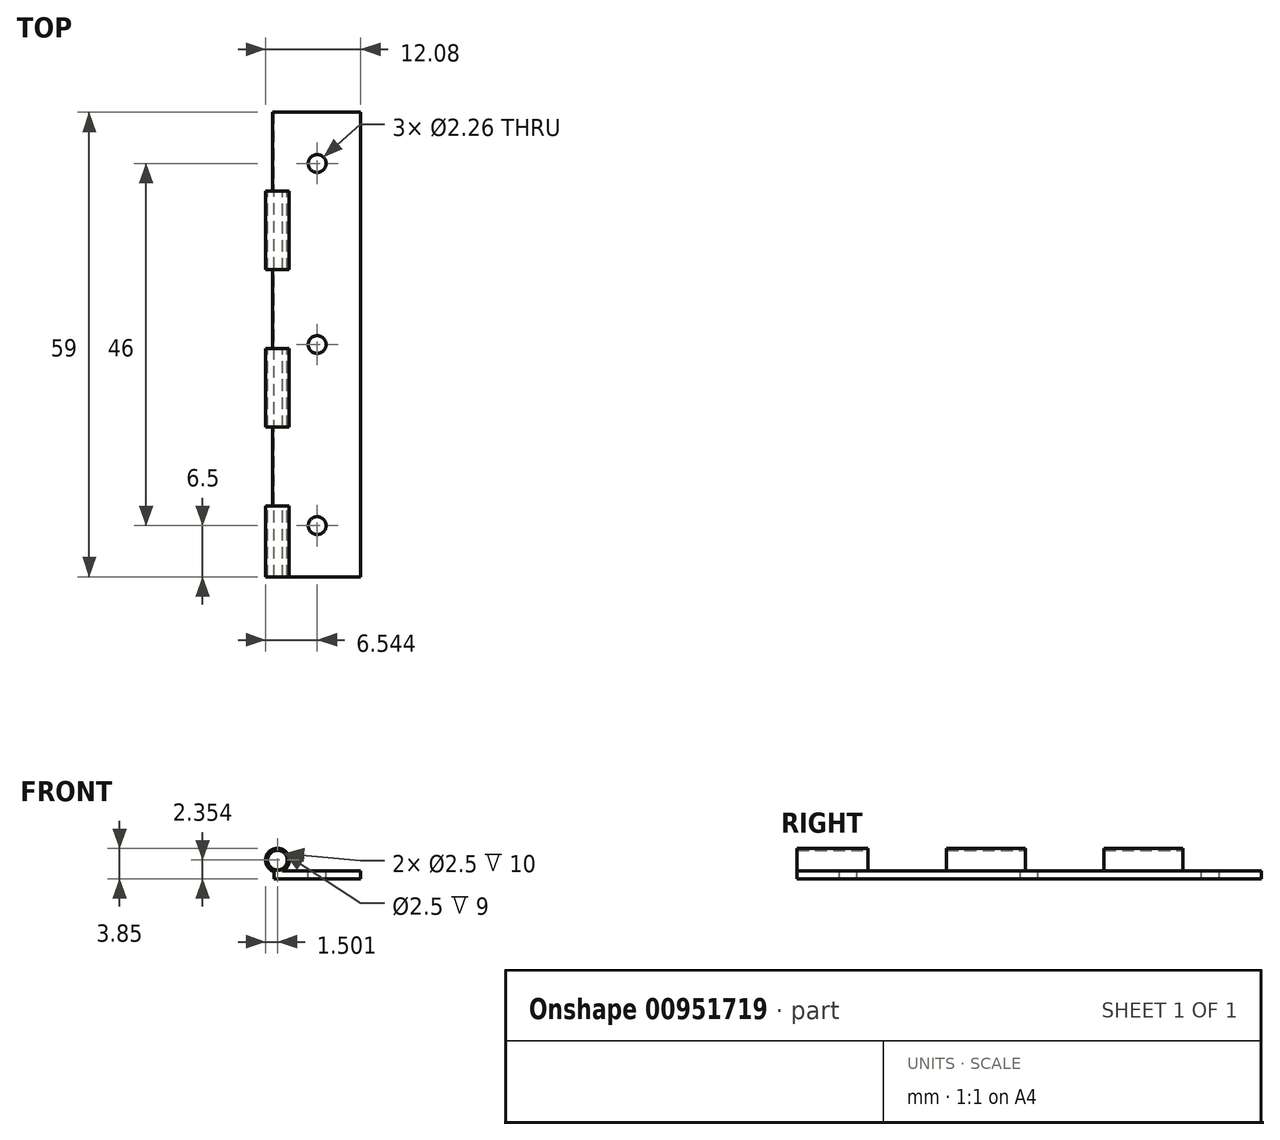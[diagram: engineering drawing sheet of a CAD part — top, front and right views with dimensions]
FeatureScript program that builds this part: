
annotation { "Feature Type Name" : "Feature", "Feature Type Description" : "" }
export const myFeature = defineFeature(function(context is Context, id is Id, definition is map)
    precondition{}
    {
        {
            var Q0;
            Q0=qCreatedBy(makeId("Front.planeOp"),FACE);
            var sketch = newSketch(context, id + "F0", { "sketchPlane" : qUnion([Q0])});
            skLineSegment(sketch, "E0.bottom", {"start": v(0, 0) * mm, "end": v(11, 0) * mm});
            skLineSegment(sketch, "E0.top", {"start": v(0, 1) * mm, "end": v(11, 1) * mm});
            skLineSegment(sketch, "E0.left", {"start": v(0, 0) * mm, "end": v(0, 1) * mm});
            skLineSegment(sketch, "E0.right", {"start": v(11, 0) * mm, "end": v(11, 1) * mm});
            skCircle(sketch, "E1", {"center": v(0.42, 2.35) * mm, "radius": 1.5 * mm});
            skCircle(sketch, "E2", {"center": v(0.42, 2.35) * mm, "radius": 1.25 * mm});
            skSolve(sketch);
        }
        {
            var Q0;
            Q0=makeQuery(id+"F0.imprint","IMPRINT",FACE,{"disambiguationData":[TD([[makeQuery(id+"F0.imprint","IMPRINT",EDGE,{"derivedFrom":sQuery(id+"F0.wireOp",EDGE,"E0.bottom")}),1.0]])]});
            var Q1;
            Q1=makeQuery(id+"F0.imprint","IMPRINT",FACE,{"disambiguationData":[TD([[makeQuery(id+"F0.imprint","IMPRINT",EDGE,{"derivedFrom":sQuery(id+"F0.wireOp",EDGE,"E1")}),1.0]])]});
            var Q2;
            Q2=makeQuery(id+"F0.imprint","IMPRINT",FACE,{"disambiguationData":[TD([[makeQuery(id+"F0.imprint","IMPRINT",EDGE,{"derivedFrom":sQuery(id+"F0.wireOp",EDGE,"E2")}),-1.0]])]});
            extrude(context, id + "F1", {"entities" : qUnion([Q0, Q1, Q2]), "depth" : 59 * mm, "offsetDistance" : 25 * mm});
        }
        {
            var Q0;
            Q0=makeQuery(id+"F1.opExtrude","SWEPT_FACE",FACE,{"disambiguationData":[OSD([sQuery(id+"F0.wireOp",EDGE,"E0.right")])]});
            var sketch = newSketch(context, id + "F2", { "sketchPlane" : qUnion([Q0])});
            skLineSegment(sketch, "E3.bottom", {"start": v(-50, 1) * mm, "end": v(-40, 1) * mm});
            skLineSegment(sketch, "E3.top", {"start": v(-50, 8) * mm, "end": v(-40, 8) * mm});
            skLineSegment(sketch, "E3.left", {"start": v(-50, 1) * mm, "end": v(-50, 8) * mm});
            skLineSegment(sketch, "E3.right", {"start": v(-40, 1) * mm, "end": v(-40, 8) * mm});
            skLineSegment(sketch, "E4.bottom", {"start": v(-30, 1) * mm, "end": v(-20, 1) * mm});
            skLineSegment(sketch, "E4.top", {"start": v(-30, 8.11) * mm, "end": v(-20, 8.11) * mm});
            skLineSegment(sketch, "E4.left", {"start": v(-30, 1) * mm, "end": v(-30, 8.11) * mm});
            skLineSegment(sketch, "E4.right", {"start": v(-20, 1) * mm, "end": v(-20, 8.11) * mm});
            skLineSegment(sketch, "E5.bottom", {"start": v(-10, 1) * mm, "end": v(0, 1) * mm});
            skLineSegment(sketch, "E5.top", {"start": v(-10, 8.11) * mm, "end": v(0, 8.11) * mm});
            skLineSegment(sketch, "E5.left", {"start": v(-10, 1) * mm, "end": v(-10, 8.11) * mm});
            skLineSegment(sketch, "E5.right", {"start": v(0, 1) * mm, "end": v(0, 8.11) * mm});
            skSolve(sketch);
        }
        {
            var Q0;
            Q0=makeQuery(id+"F2.imprint","IMPRINT",FACE,{"disambiguationData":[TD([[makeQuery(id+"F2.imprint","IMPRINT",EDGE,{"derivedFrom":sQuery(id+"F2.wireOp",EDGE,"E3.bottom")}),1.0]])]});
            var Q1;
            Q1=makeQuery(id+"F2.imprint","IMPRINT",FACE,{"disambiguationData":[TD([[makeQuery(id+"F2.imprint","IMPRINT",EDGE,{"derivedFrom":sQuery(id+"F2.wireOp",EDGE,"E4.bottom")}),1.0]])]});
            var Q2;
            Q2=makeQuery(id+"F2.imprint","IMPRINT",FACE,{"disambiguationData":[TD([[makeQuery(id+"F2.imprint","IMPRINT",EDGE,{"derivedFrom":sQuery(id+"F2.wireOp",EDGE,"E5.bottom")}),1.0]])]});
            extrude(context, id + "F3", {"entities" : qUnion([Q0, Q1, Q2]), "operationType" : NewBodyOperationType.REMOVE, "endBound" : BoundingType.THROUGH_ALL, "oppositeDirection" : true, "depth" : 25 * mm, "offsetDistance" : 25 * mm});
        }
        {
            var Q0;
            Q0=makeQuery(id+"F3.boolean.opBoolean","MERGE",FACE,{"derivedFrom":[makeQuery(id+"F1.opExtrude","SWEPT_FACE",FACE,{"disambiguationData":[OSD([sQuery(id+"F0.wireOp",EDGE,"E0.top")])]})],"fromTools":[makeQuery(id+"F3.opExtrude","SWEPT_FACE",FACE,{"disambiguationData":[OSD([sQuery(id+"F2.wireOp",EDGE,"E3.bottom")])]}),makeQuery(id+"F3.opExtrude","SWEPT_FACE",FACE,{"disambiguationData":[OSD([sQuery(id+"F2.wireOp",EDGE,"E4.bottom")])]}),makeQuery(id+"F3.opExtrude","SWEPT_FACE",FACE,{"disambiguationData":[OSD([sQuery(id+"F2.wireOp",EDGE,"E5.bottom")])]})]});
            var sketch = newSketch(context, id + "F4", { "sketchPlane" : qUnion([Q0])});
            skPoint(sketch, "E6", {"position": v(5.46, -6.5) * mm});
            skPoint(sketch, "E7", {"position": v(5.46, -29.5) * mm});
            skPoint(sketch, "E8", {"position": v(5.46, -52.5) * mm});
            skSolve(sketch);
        }
        {
            var Q0;
            Q0=sQuery(id+"F4.wireOp",VERTEX,"E6");
            var Q1;
            Q1=sQuery(id+"F4.wireOp",VERTEX,"E7");
            var Q2;
            Q2=sQuery(id+"F4.wireOp",VERTEX,"E8");
            var Q3;
            Q3=makeQuery(id+"F1.opExtrude","SWEPT_BODY",BODY,{"disambiguationData":[OSD([sQuery(id+"F0.wireOp",EDGE,"E0.bottom"),sQuery(id+"F0.wireOp",EDGE,"E0.top"),sQuery(id+"F0.wireOp",EDGE,"E0.left"),sQuery(id+"F0.wireOp",EDGE,"E0.right"),sQuery(id+"F0.wireOp",EDGE,"E1"),sQuery(id+"F0.wireOp",EDGE,"E2")])]});
            hole(context, id + "F5", {"style" : HoleStyle.SIMPLE, "endStyle" : HoleEndStyle.THROUGH, "standardTappedOrClearance" : lookupTablePath({ "fit" : "Normal (ASME)", "standard" : "ANSI", "size" : "#1", "type" : "Clearance" }), "standardBlindInLast" : lookupTablePath({ "fit" : "Normal", "standard" : "ANSI", "engagement" : "75%", "pitch" : "64 tpi", "size" : "#1", "type" : "Clearance & tapped" }), "holeDiameter" : 2.26 * mm, "majorDiameter" : 5 * mm, "isTappedThrough" : true, "tappedDepth" : 12 * mm, "tapClearance" : 3, "locations" : qUnion([Q0, Q1, Q2]), "scope" : qUnion([Q3])});
        }
    });
